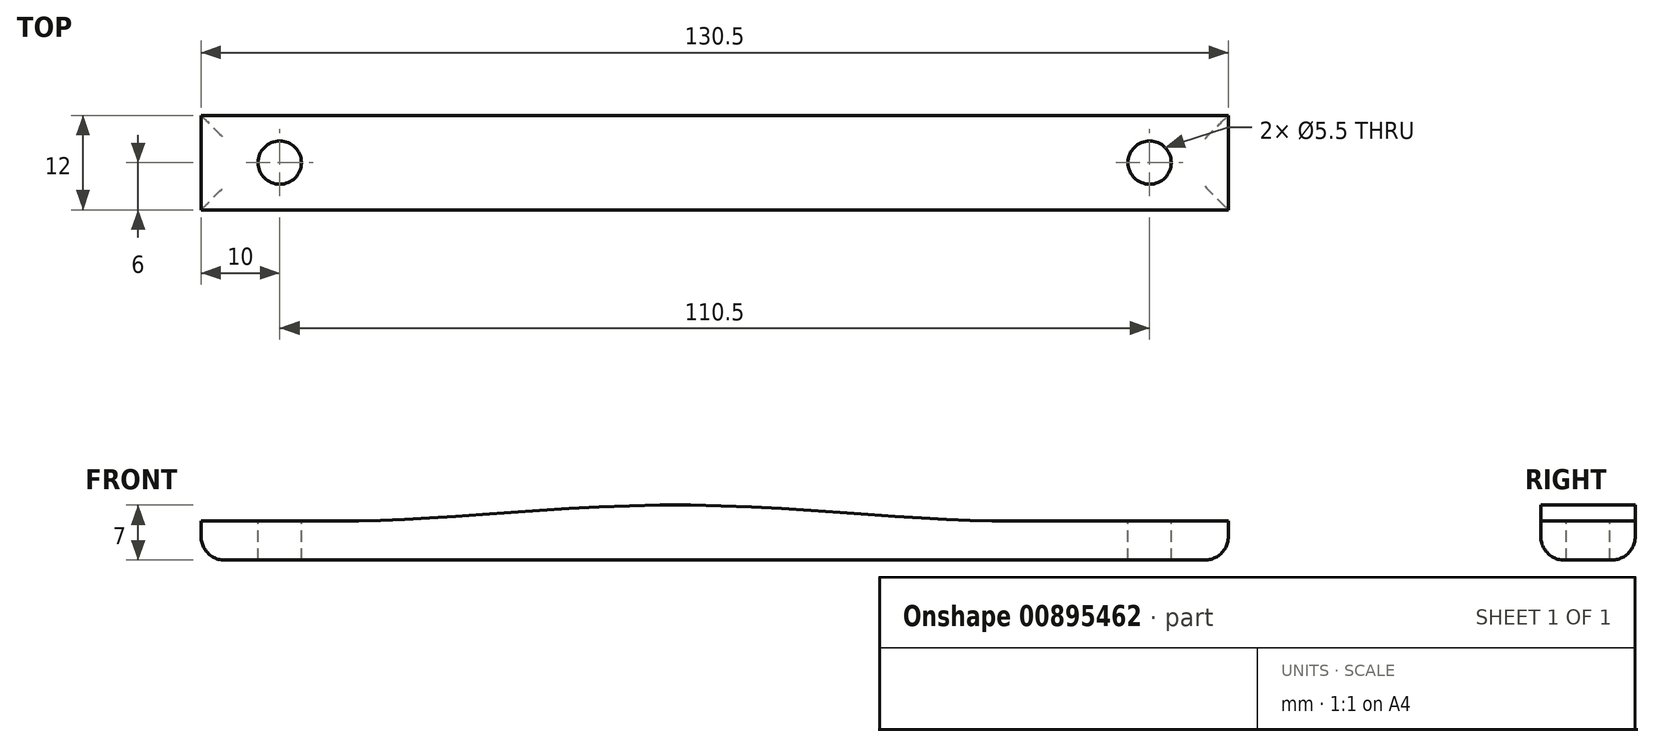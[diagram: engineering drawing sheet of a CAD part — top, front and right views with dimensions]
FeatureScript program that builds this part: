
annotation { "Feature Type Name" : "Feature", "Feature Type Description" : "" }
export const myFeature = defineFeature(function(context is Context, id is Id, definition is map)
    precondition{}
    {
        {
            var Q0;
            Q0=qCreatedBy(makeId("Front.planeOp"),FACE);
            var sketch = newSketch(context, id + "F0", { "sketchPlane" : qUnion([Q0])});
            skFitSpline(sketch, "E0", {"points": [v(-40.25, 5) * mm, v(0, 7) * mm, v(40.25, 5) * mm], "startDerivative": vector(62.72, 0) * mm, "endDerivative": vector(62.72, 0) * mm});
            skLineSegment(sketch, "E1", {"start": v(-40.25, 5) * mm, "end": v(-40.25, 0) * mm});
            skLineSegment(sketch, "E2", {"start": v(-40.25, 0) * mm, "end": v(40.25, 0) * mm});
            skLineSegment(sketch, "E3", {"start": v(40.25, 0) * mm, "end": v(40.25, 5) * mm});
            skLineSegment(sketch, "E4.bottom", {"start": v(-40.25, 5) * mm, "end": v(-60.25, 5) * mm});
            skLineSegment(sketch, "E4.top", {"start": v(-40.25, 0) * mm, "end": v(-60.25, 0) * mm});
            skLineSegment(sketch, "E4.right", {"start": v(-60.25, 5) * mm, "end": v(-60.25, 0) * mm});
            skLineSegment(sketch, "E5.bottom", {"start": v(40.25, 5) * mm, "end": v(70.25, 5) * mm});
            skLineSegment(sketch, "E5.top", {"start": v(40.25, 0) * mm, "end": v(70.25, 0) * mm});
            skLineSegment(sketch, "E5.left", {"start": v(40.25, 5) * mm, "end": v(40.25, 0) * mm});
            skLineSegment(sketch, "E5.right", {"start": v(70.25, 5) * mm, "end": v(70.25, 0) * mm});
            skSolve(sketch);
        }
        {
            var Q0;
            Q0=makeQuery(id+"F0.imprint","IMPRINT",FACE,{"disambiguationData":[TD([[makeQuery(id+"F0.imprint","IMPRINT",EDGE,{"derivedFrom":sQuery(id+"F0.wireOp",EDGE,"E4.bottom")}),1.0]])]});
            var Q1;
            Q1=makeQuery(id+"F0.imprint","IMPRINT",FACE,{"disambiguationData":[TD([[makeQuery(id+"F0.imprint","IMPRINT",EDGE,{"derivedFrom":sQuery(id+"F0.wireOp",EDGE,"E0")}),-1.0]])]});
            var Q2;
            Q2=makeQuery(id+"F0.imprint","IMPRINT",FACE,{"disambiguationData":[TD([[makeQuery(id+"F0.imprint","IMPRINT",EDGE,{"derivedFrom":sQuery(id+"F0.wireOp",EDGE,"E5.bottom")}),-1.0]])]});
            extrude(context, id + "F1", {"entities" : qUnion([Q0, Q1, Q2]), "endBound" : BoundingType.SYMMETRIC, "depth" : 12 * mm, "offsetDistance" : 25 * mm});
        }
        {
            var Q0;
            Q0=makeQuery(id+"F1.opExtrude","SWEPT_FACE",FACE,{"disambiguationData":[OSD([sQuery(id+"F0.wireOp",EDGE,"E4.bottom")])]});
            var sketch = newSketch(context, id + "F2", { "sketchPlane" : qUnion([Q0])});
            skCircle(sketch, "E6", {"center": v(-50.25, 0) * mm, "radius": 2.75 * mm});
            skCircle(sketch, "E7", {"center": v(60.25, 0) * mm, "radius": 2.75 * mm});
            skSolve(sketch);
        }
        {
            var Q0;
            Q0=makeQuery(id+"F2.imprint","IMPRINT",FACE,{"disambiguationData":[TD([[makeQuery(id+"F2.imprint","IMPRINT",EDGE,{"derivedFrom":sQuery(id+"F2.wireOp",EDGE,"E6")}),1.0]])]});
            var Q1;
            Q1=makeQuery(id+"F2.imprint","IMPRINT",FACE,{"disambiguationData":[TD([[makeQuery(id+"F2.imprint","IMPRINT",EDGE,{"derivedFrom":sQuery(id+"F2.wireOp",EDGE,"E7")}),1.0]])]});
            extrude(context, id + "F3", {"entities" : qUnion([Q0, Q1]), "operationType" : NewBodyOperationType.REMOVE, "endBound" : BoundingType.THROUGH_ALL, "oppositeDirection" : true, "depth" : 25 * mm, "offsetDistance" : 25 * mm});
        }
        {
            var Q0;
            Q0=makeQuery(id+"F1.opExtrude","SWEPT_EDGE",EDGE,{"disambiguationData":[OSD([sQuery(id+"F0.wireOp",EDGE,"E4.top"),sQuery(id+"F0.wireOp",EDGE,"E4.right")])]});
            var Q1;
            Q1=makeQuery(id+"F1.opExtrude","CAP_EDGE",EDGE,{"disambiguationData":[OSD([sQuery(id+"F0.wireOp",EDGE,"E2"),sQuery(id+"F0.wireOp",EDGE,"E4.top"),sQuery(id+"F0.wireOp",EDGE,"E5.top")])],"isStart":false});
            var Q2;
            Q2=makeQuery(id+"F1.opExtrude","CAP_EDGE",EDGE,{"disambiguationData":[OSD([sQuery(id+"F0.wireOp",EDGE,"E2"),sQuery(id+"F0.wireOp",EDGE,"E4.top"),sQuery(id+"F0.wireOp",EDGE,"E5.top")])],"isStart":true});
            var Q3;
            Q3=makeQuery(id+"F1.opExtrude","SWEPT_EDGE",EDGE,{"disambiguationData":[OSD([sQuery(id+"F0.wireOp",EDGE,"E5.top"),sQuery(id+"F0.wireOp",EDGE,"E5.right")])]});
            fillet(context, id + "F4", {"entities" : qUnion([Q0, Q1, Q2, Q3]), "radius" : 3 * mm, "tangentPropagation" : true, "allowEdgeOverflow" : false});
        }
    });
